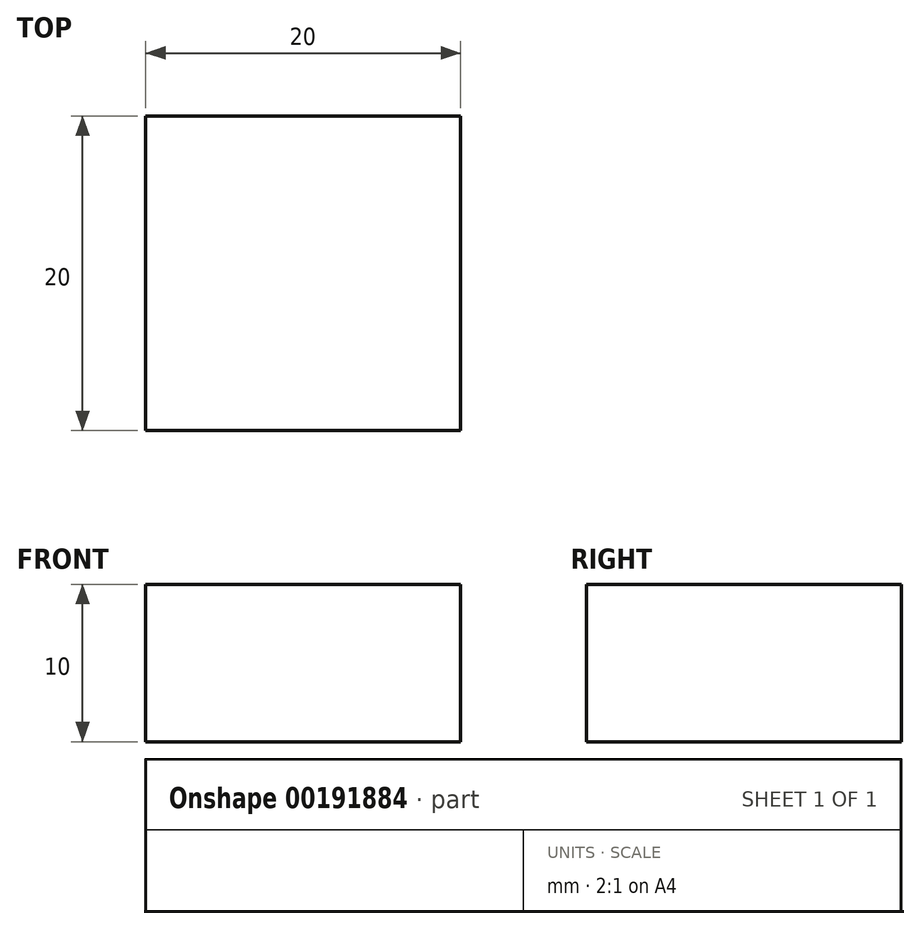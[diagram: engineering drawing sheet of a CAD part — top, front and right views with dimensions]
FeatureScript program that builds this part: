
annotation { "Feature Type Name" : "Feature", "Feature Type Description" : "" }
export const myFeature = defineFeature(function(context is Context, id is Id, definition is map)
    precondition{}
    {
        {
            var Q0;
            Q0=qCreatedBy(makeId("Top.planeOp"),FACE);
            var sketch = newSketch(context, id + "F0", { "sketchPlane" : qUnion([Q0])});
            skLineSegment(sketch, "E0.bottom", {"start": v(10, -10) * mm, "end": v(-10, -10) * mm});
            skLineSegment(sketch, "E0.top", {"start": v(10, 10) * mm, "end": v(-10, 10) * mm});
            skLineSegment(sketch, "E0.left", {"start": v(10, -10) * mm, "end": v(10, 10) * mm});
            skLineSegment(sketch, "E0.right", {"start": v(-10, -10) * mm, "end": v(-10, 10) * mm});
            skPoint(sketch, "E0.middle", {"position": v(0, 0) * mm});
            skSolve(sketch);
        }
        {
            var Q0;
            Q0=makeQuery(id+"F0.imprint","IMPRINT",FACE,{"disambiguationData":[TD([[makeQuery(id+"F0.imprint","IMPRINT",EDGE,{"derivedFrom":sQuery(id+"F0.wireOp",EDGE,"E0.bottom")}),-1.0]])]});
            extrude(context, id + "F1", {"entities" : qUnion([Q0]), "depth" : 10 * mm, "offsetDistance" : 25 * mm});
        }
    });
